# Revit family: RN 82130 Optipress-Rubinetto a sfera
name_source: partatom
category: Rohrzubehör
units: mm (PartAtom-declared; Revit-internal decimal feet)

## family parameters
Arbeitsebenenbasiert = Nein
Beim Laden mit Abzugskörper schneiden = Nein
Bemaßung runder Anschluss = Durchmesser verwenden
Gemeinsam genutzt = Nein
Immer vertikal = Ja
Teiletyp = Ventil - Zerlegung in

## types (3) — shared parameters
1.010.00.2 Number of the part of the guideline = 2
1.010.00.3 Issue date (month) of the guideline = 201601
1.010.00.4 Manufacturer name = R. Nussbaum AG
1.010.00.5 Revision date of the file = 20190514
1.100.00.3 Sort number for display sequence = 4
1.100.00.4 Product designation = Absperr- und Regelarmaturen
1.960/3L.00.8 Link (URL) = https://www.nussbaum.ch
2.700.00.4 valve assembly type = 11
2.700.00.7 maximum operating temperature TB [°C] = 110
2.700.00.8 maximum operating pressure(working pressure) ps [1.0 · 102 Pa] = 16
CONNECTOR0_dX_01 = 28 mm
CONNECTOR0_ref_dX = 28 mm
Connector Visibility = Nein
EnclosingSpace Visibility = Nein
Hersteller = R. Nussbaum AG
URL = https://www.nussbaum.ch

## per-type parameters (varying)
| type | 1.800.00.3 BS number | 1.810.00.3 Manufacturer’s reference number | 1.810.00.4 DATANORM number | 1.810.00.6 GTIN number | 2.700.00.26 product description | 2.700.00.5 nominal size DN | 2.700.00.6 kvs-value [m3/h] | CONNECTOR0_DIAMETER_dX_0r | CONNECTOR0_dX_00 | CONNECTOR1_DIAMETER_dX_0r | CONNECTOR1_dX_00 | CONNECTOR1_dX_01 | CONNECTOR1_ref_dX | Modell | R. Nussbaum AG 82130.22 en Visibility | R. Nussbaum AG 82130.23 en Visibility | R. Nussbaum AG 82130.24 en Visibility | Typenkommentare |
| DN 12 | 0040310000000000000000000000020070000000000000000100000000 | 82130.22 | 82130.22 | 7612945815408 | 82130.22, Optipress-Kugelhahn, mit Verschraubung, mit Flügelgriff, DN=12x20 | 12 | 10.3 | 12 mm  [stored 0.0393701 ft] | 50 mm | 12 mm  [stored 0.0393701 ft] | 35 mm | 43 mm | 35 mm | 82130.22 | Ja | Nein | Nein | Optipress-Rubinetto a sfera DN 12 |
| DN 15 | 0040310000000000000000000000020070000000000000000200000000 | 82130.23 | 82130.23 | 7612945815415 | 82130.23, Optipress-Kugelhahn, mit Verschraubung, mit Flügelgriff, DN=15 | 15 | 33 | 15 mm  [stored 0.0492126 ft] | 50 mm | 15 mm  [stored 0.0492126 ft] | 35 mm | 43 mm | 35 mm | 82130.23 | Nein | Ja | Nein | Optipress-Rubinetto a sfera DN 15 |
| DN 20 | 0040310000000000000000000000020070000000000000000300000000 | 82130.24 | 82130.24 | 7612945815422 | 82130.24, Optipress-Kugelhahn, mit Verschraubung, mit Flügelgriff, DN=20 | 20 | 47 | 20 mm | 52 mm | 20 mm | 36 mm | 44 mm | 36 mm | 82130.24 | Nein | Nein | Ja | Optipress-Rubinetto a sfera DN 20 |

note: [stored X ft] marks values corroborated as IEEE doubles in the binary element streams (Revit-internal decimal feet)

## geometry (parser evidence)
native form markers: Sweep x2
no freeform markers — native parametric forms only
